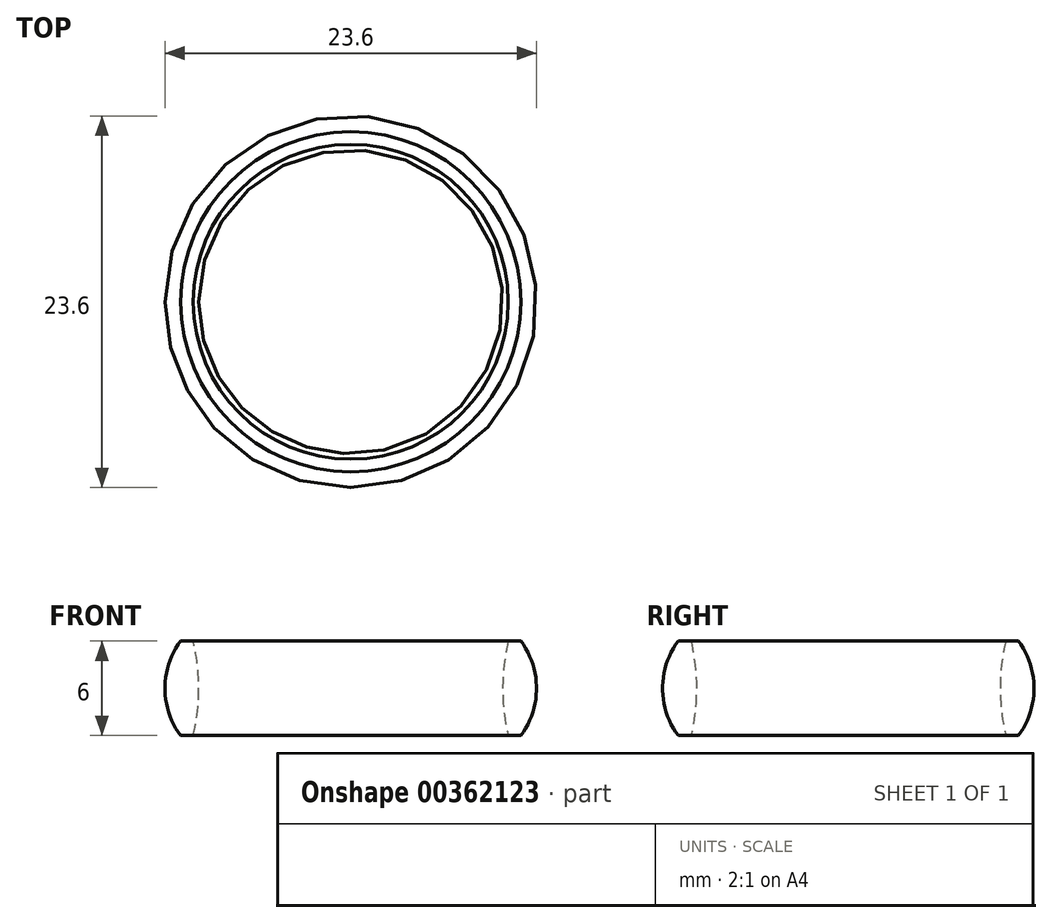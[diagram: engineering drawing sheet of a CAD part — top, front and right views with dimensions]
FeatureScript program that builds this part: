
annotation { "Feature Type Name" : "Feature", "Feature Type Description" : "" }
export const myFeature = defineFeature(function(context is Context, id is Id, definition is map)
    precondition{}
    {
        {
            var Q0;
            Q0=qCreatedBy(makeId("Front.planeOp"),FACE);
            var sketch = newSketch(context, id + "F0", { "sketchPlane" : qUnion([Q0])});
            skArc(sketch, "E0", {"start": v(-10.8, 6) * mm, "mid": v(-11.8, 3) * mm, "end": v(-10.8, 0) * mm});
            skArc(sketch, "E1", {"start": v(-10, 0) * mm, "mid": v(-9.65, 3) * mm, "end": v(-10, 6) * mm});
            skLineSegment(sketch, "E2", {"start": v(-10.8, 6) * mm, "end": v(-10, 6) * mm});
            skLineSegment(sketch, "E3", {"start": v(-10, 0) * mm, "end": v(-10.8, 0) * mm});
            skLineSegment(sketch, "E4", {"start": v(0, 0) * mm, "end": v(0, 6) * mm, "construction": true});
            skArc(sketch, "E5", {"start": v(-11.38, 1) * mm, "mid": v(-11.38, 1.6) * mm, "end": v(-11.72, 2.1) * mm});
            skArc(sketch, "E6", {"start": v(-11.72, 3.9) * mm, "mid": v(-11.38, 4.4) * mm, "end": v(-11.38, 5) * mm});
            skLineSegment(sketch, "E7", {"start": v(-6.8, 3) * mm, "end": v(0, 3) * mm, "construction": true});
            skSolve(sketch);
        }
        {
            var Q0;
            Q0=makeQuery(id+"F0.imprint","IMPRINT",FACE,{"disambiguationData":[TD([[makeQuery(id+"F0.imprint","IMPRINT",EDGE,{"derivedFrom":sQuery(id+"F0.wireOp",EDGE,"E0")}),1.0]])]});
            var Q1;
            {var subQ0=sQuery(id+"F0.wireOp",EDGE,"E6");Q1=makeQuery(id+"F0.imprint","IMPRINT",FACE,{"disambiguationData":[TD([[makeQuery(id+"F0.imprint","IMPRINT",EDGE,{"derivedFrom":subQ0}),1.0]])]});}
            var Q2;
            {var subQ0=sQuery(id+"F0.wireOp",EDGE,"E5");Q2=makeQuery(id+"F0.imprint","IMPRINT",FACE,{"disambiguationData":[TD([[makeQuery(id+"F0.imprint","IMPRINT",EDGE,{"derivedFrom":subQ0}),1.0]])]});}
            var Q3;
            Q3=sQuery(id+"F0.wireOp",EDGE,"E4");
            revolve(context, id + "F1", {"surfaceOperationType" : NewSurfaceOperationType.NEW, "entities" : qUnion([Q0, Q1, Q2]), "axis" : qUnion([Q3]), "revolveType" : RevolveType.FULL});
        }
    });
